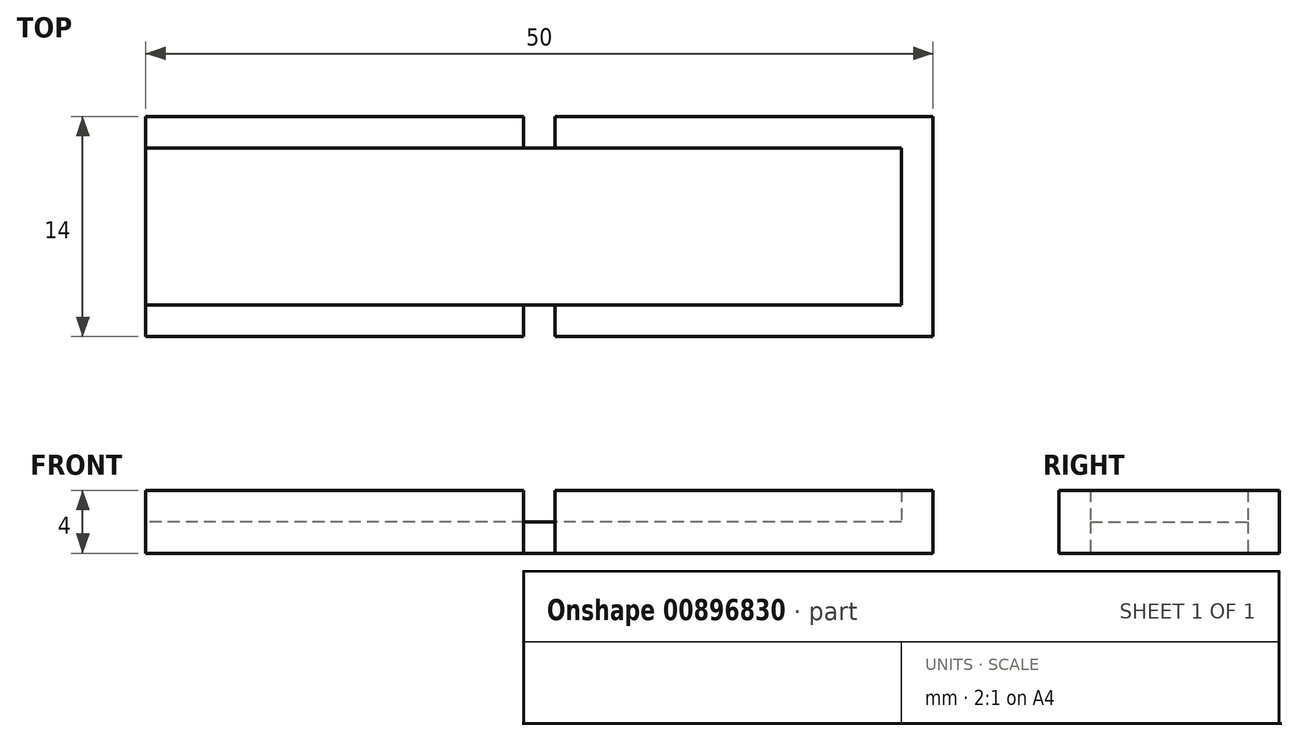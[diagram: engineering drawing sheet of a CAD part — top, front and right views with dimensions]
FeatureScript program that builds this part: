
annotation { "Feature Type Name" : "Feature", "Feature Type Description" : "" }
export const myFeature = defineFeature(function(context is Context, id is Id, definition is map)
    precondition{}
    {
        {
            var Q0;
            Q0=qCreatedBy(makeId("Top.planeOp"),FACE);
            var sketch = newSketch(context, id + "F0", { "sketchPlane" : qUnion([Q0])});
            skLineSegment(sketch, "E0.bottom", {"start": v(-25, 7) * mm, "end": v(25, 7) * mm});
            skLineSegment(sketch, "E0.top", {"start": v(-25, -7) * mm, "end": v(25, -7) * mm});
            skLineSegment(sketch, "E0.left", {"start": v(-25, 7) * mm, "end": v(-25, -7) * mm});
            skLineSegment(sketch, "E0.right", {"start": v(25, 7) * mm, "end": v(25, -7) * mm});
            skPoint(sketch, "E0.middle", {"position": v(0, 0) * mm});
            skLineSegment(sketch, "E1.bottom", {"start": v(-25, 5) * mm, "end": v(25, 5) * mm});
            skLineSegment(sketch, "E1.top", {"start": v(-25, -5) * mm, "end": v(25, -5) * mm});
            skLineSegment(sketch, "E1.left", {"start": v(-25, 5) * mm, "end": v(-25, -5) * mm});
            skLineSegment(sketch, "E1.right", {"start": v(25, 5) * mm, "end": v(25, -5) * mm});
            skLineSegment(sketch, "E2.bottom", {"start": v(25, 7) * mm, "end": v(23, 7) * mm});
            skLineSegment(sketch, "E2.top", {"start": v(25, -7) * mm, "end": v(23, -7) * mm});
            skLineSegment(sketch, "E2.right", {"start": v(23, 7) * mm, "end": v(23, -7) * mm});
            skLineSegment(sketch, "E3.bottom", {"start": v(-1, 7) * mm, "end": v(1, 7) * mm});
            skLineSegment(sketch, "E3.top", {"start": v(-1, -7) * mm, "end": v(1, -7) * mm});
            skLineSegment(sketch, "E3.left", {"start": v(-1, 7) * mm, "end": v(-1, -7) * mm});
            skLineSegment(sketch, "E3.right", {"start": v(1, 7) * mm, "end": v(1, -7) * mm});
            skSolve(sketch);
        }
        {
            var Q0;
            {var subQ0=sQuery(id+"F0.wireOp",EDGE,"E1.bottom");var subQ1=sQuery(id+"F0.wireOp",EDGE,"E0.left");var subQ2=makeQuery(id+"F0.imprint","INTERSECT",VERTEX,{"derivedFrom":[subQ1,subQ0]});Q0=makeQuery(id+"F0.imprint","IMPRINT",FACE,{"disambiguationData":[TD([[makeQuery(id+"F0.imprint","IMPRINT",EDGE,{"disambiguationData":[TD([[subQ2,-1.0]])],"derivedFrom":subQ1}),1.0]])]});}
            var Q1;
            {var subQ0=sQuery(id+"F0.wireOp",EDGE,"E0.left");var subQ1=sQuery(id+"F0.wireOp",EDGE,"E0.top");var subQ2=makeQuery(id+"F0.imprint","INTERSECT",VERTEX,{"derivedFrom":[subQ1,subQ0]});Q1=makeQuery(id+"F0.imprint","IMPRINT",FACE,{"disambiguationData":[TD([[makeQuery(id+"F0.imprint","IMPRINT",EDGE,{"disambiguationData":[TD([[subQ2,-1.0]])],"derivedFrom":subQ1}),1.0]])]});}
            var Q2;
            {var subQ0=sQuery(id+"F0.wireOp",EDGE,"E3.right");var subQ1=sQuery(id+"F0.wireOp",EDGE,"E1.bottom");var subQ2=makeQuery(id+"F0.imprint","INTERSECT",VERTEX,{"derivedFrom":[subQ1,subQ0]});Q2=makeQuery(id+"F0.imprint","IMPRINT",FACE,{"disambiguationData":[TD([[makeQuery(id+"F0.imprint","IMPRINT",EDGE,{"disambiguationData":[TD([[subQ2,1.0]])],"derivedFrom":subQ1}),-1.0]])]});}
            var Q3;
            {var subQ0=sQuery(id+"F0.wireOp",EDGE,"E2.right");var subQ1=sQuery(id+"F0.wireOp",EDGE,"E0.top");var subQ2=makeQuery(id+"F0.imprint","INTERSECT",VERTEX,{"derivedFrom":[subQ1,subQ0]});Q3=makeQuery(id+"F0.imprint","IMPRINT",FACE,{"disambiguationData":[TD([[makeQuery(id+"F0.imprint","IMPRINT",EDGE,{"disambiguationData":[TD([[subQ2,1.0]])],"derivedFrom":subQ1}),1.0]])]});}
            var Q4;
            {var subQ0=sQuery(id+"F0.wireOp",EDGE,"E0.right");var subQ1=sQuery(id+"F0.wireOp",EDGE,"E0.top");var subQ2=makeQuery(id+"F0.imprint","INTERSECT",VERTEX,{"derivedFrom":[subQ1,subQ0]});Q4=makeQuery(id+"F0.imprint","IMPRINT",FACE,{"disambiguationData":[TD([[makeQuery(id+"F0.imprint","IMPRINT",EDGE,{"disambiguationData":[TD([[subQ2,1.0]])],"derivedFrom":subQ1}),1.0]])]});}
            var Q5;
            {var subQ0=sQuery(id+"F0.wireOp",EDGE,"E1.bottom");var subQ1=sQuery(id+"F0.wireOp",EDGE,"E0.right");var subQ2=makeQuery(id+"F0.imprint","INTERSECT",VERTEX,{"derivedFrom":[subQ1,subQ0]});Q5=makeQuery(id+"F0.imprint","IMPRINT",FACE,{"disambiguationData":[TD([[makeQuery(id+"F0.imprint","IMPRINT",EDGE,{"disambiguationData":[TD([[subQ2,-1.0]])],"derivedFrom":subQ1}),-1.0]])]});}
            var Q6;
            {var subQ0=sQuery(id+"F0.wireOp",EDGE,"E3.right");var subQ1=sQuery(id+"F0.wireOp",EDGE,"E1.bottom");var subQ2=makeQuery(id+"F0.imprint","INTERSECT",VERTEX,{"derivedFrom":[subQ1,subQ0]});Q6=makeQuery(id+"F0.imprint","IMPRINT",FACE,{"disambiguationData":[TD([[makeQuery(id+"F0.imprint","IMPRINT",EDGE,{"disambiguationData":[TD([[subQ2,-1.0]])],"derivedFrom":subQ1}),-1.0]])]});}
            var Q7;
            {var subQ0=sQuery(id+"F0.wireOp",EDGE,"E3.right");var subQ1=sQuery(id+"F0.wireOp",EDGE,"E0.bottom");var subQ2=makeQuery(id+"F0.imprint","INTERSECT",VERTEX,{"derivedFrom":[subQ1,subQ0]});Q7=makeQuery(id+"F0.imprint","IMPRINT",FACE,{"disambiguationData":[TD([[makeQuery(id+"F0.imprint","IMPRINT",EDGE,{"disambiguationData":[TD([[subQ2,-1.0]])],"derivedFrom":subQ1}),-1.0]])]});}
            var Q8;
            {var subQ0=sQuery(id+"F0.wireOp",EDGE,"E0.left");var subQ1=sQuery(id+"F0.wireOp",EDGE,"E0.bottom");var subQ2=makeQuery(id+"F0.imprint","INTERSECT",VERTEX,{"derivedFrom":[subQ1,subQ0]});Q8=makeQuery(id+"F0.imprint","IMPRINT",FACE,{"disambiguationData":[TD([[makeQuery(id+"F0.imprint","IMPRINT",EDGE,{"disambiguationData":[TD([[subQ2,-1.0]])],"derivedFrom":subQ1}),-1.0]])]});}
            var Q9;
            {var subQ0=sQuery(id+"F0.wireOp",EDGE,"E0.right");var subQ1=sQuery(id+"F0.wireOp",EDGE,"E0.bottom");var subQ2=makeQuery(id+"F0.imprint","INTERSECT",VERTEX,{"derivedFrom":[subQ1,subQ0]});Q9=makeQuery(id+"F0.imprint","IMPRINT",FACE,{"disambiguationData":[TD([[makeQuery(id+"F0.imprint","IMPRINT",EDGE,{"disambiguationData":[TD([[subQ2,1.0]])],"derivedFrom":subQ1}),-1.0]])]});}
            extrude(context, id + "F1", {"entities" : qUnion([Q0, Q1, Q2, Q3, Q4, Q5, Q6, Q7, Q8, Q9]), "depth" : 2 * mm, "offsetDistance" : 25 * mm});
        }
        {
            var Q0;
            {var subQ0=sQuery(id+"F0.wireOp",EDGE,"E2.right");var subQ1=sQuery(id+"F0.wireOp",EDGE,"E0.top");var subQ2=makeQuery(id+"F0.imprint","INTERSECT",VERTEX,{"derivedFrom":[subQ1,subQ0]});Q0=makeQuery(id+"F0.imprint","IMPRINT",FACE,{"disambiguationData":[TD([[makeQuery(id+"F0.imprint","IMPRINT",EDGE,{"disambiguationData":[TD([[subQ2,1.0]])],"derivedFrom":subQ1}),1.0]])]});}
            var Q1;
            {var subQ0=sQuery(id+"F0.wireOp",EDGE,"E0.right");var subQ1=sQuery(id+"F0.wireOp",EDGE,"E0.top");var subQ2=makeQuery(id+"F0.imprint","INTERSECT",VERTEX,{"derivedFrom":[subQ1,subQ0]});Q1=makeQuery(id+"F0.imprint","IMPRINT",FACE,{"disambiguationData":[TD([[makeQuery(id+"F0.imprint","IMPRINT",EDGE,{"disambiguationData":[TD([[subQ2,1.0]])],"derivedFrom":subQ1}),1.0]])]});}
            var Q2;
            {var subQ0=sQuery(id+"F0.wireOp",EDGE,"E1.bottom");var subQ1=sQuery(id+"F0.wireOp",EDGE,"E0.right");var subQ2=makeQuery(id+"F0.imprint","INTERSECT",VERTEX,{"derivedFrom":[subQ1,subQ0]});Q2=makeQuery(id+"F0.imprint","IMPRINT",FACE,{"disambiguationData":[TD([[makeQuery(id+"F0.imprint","IMPRINT",EDGE,{"disambiguationData":[TD([[subQ2,-1.0]])],"derivedFrom":subQ1}),-1.0]])]});}
            var Q3;
            {var subQ0=sQuery(id+"F0.wireOp",EDGE,"E0.right");var subQ1=sQuery(id+"F0.wireOp",EDGE,"E0.bottom");var subQ2=makeQuery(id+"F0.imprint","INTERSECT",VERTEX,{"derivedFrom":[subQ1,subQ0]});Q3=makeQuery(id+"F0.imprint","IMPRINT",FACE,{"disambiguationData":[TD([[makeQuery(id+"F0.imprint","IMPRINT",EDGE,{"disambiguationData":[TD([[subQ2,1.0]])],"derivedFrom":subQ1}),-1.0]])]});}
            var Q4;
            {var subQ0=sQuery(id+"F0.wireOp",EDGE,"E3.right");var subQ1=sQuery(id+"F0.wireOp",EDGE,"E0.bottom");var subQ2=makeQuery(id+"F0.imprint","INTERSECT",VERTEX,{"derivedFrom":[subQ1,subQ0]});Q4=makeQuery(id+"F0.imprint","IMPRINT",FACE,{"disambiguationData":[TD([[makeQuery(id+"F0.imprint","IMPRINT",EDGE,{"disambiguationData":[TD([[subQ2,-1.0]])],"derivedFrom":subQ1}),-1.0]])]});}
            var Q5;
            {var subQ0=sQuery(id+"F0.wireOp",EDGE,"E0.left");var subQ1=sQuery(id+"F0.wireOp",EDGE,"E0.bottom");var subQ2=makeQuery(id+"F0.imprint","INTERSECT",VERTEX,{"derivedFrom":[subQ1,subQ0]});Q5=makeQuery(id+"F0.imprint","IMPRINT",FACE,{"disambiguationData":[TD([[makeQuery(id+"F0.imprint","IMPRINT",EDGE,{"disambiguationData":[TD([[subQ2,-1.0]])],"derivedFrom":subQ1}),-1.0]])]});}
            var Q6;
            {var subQ0=sQuery(id+"F0.wireOp",EDGE,"E0.left");var subQ1=sQuery(id+"F0.wireOp",EDGE,"E0.top");var subQ2=makeQuery(id+"F0.imprint","INTERSECT",VERTEX,{"derivedFrom":[subQ1,subQ0]});Q6=makeQuery(id+"F0.imprint","IMPRINT",FACE,{"disambiguationData":[TD([[makeQuery(id+"F0.imprint","IMPRINT",EDGE,{"disambiguationData":[TD([[subQ2,-1.0]])],"derivedFrom":subQ1}),1.0]])]});}
            extrude(context, id + "F2", {"entities" : qUnion([Q0, Q1, Q2, Q3, Q4, Q5, Q6]), "operationType" : NewBodyOperationType.ADD, "depth" : 4 * mm, "offsetDistance" : 25 * mm});
        }
    });
